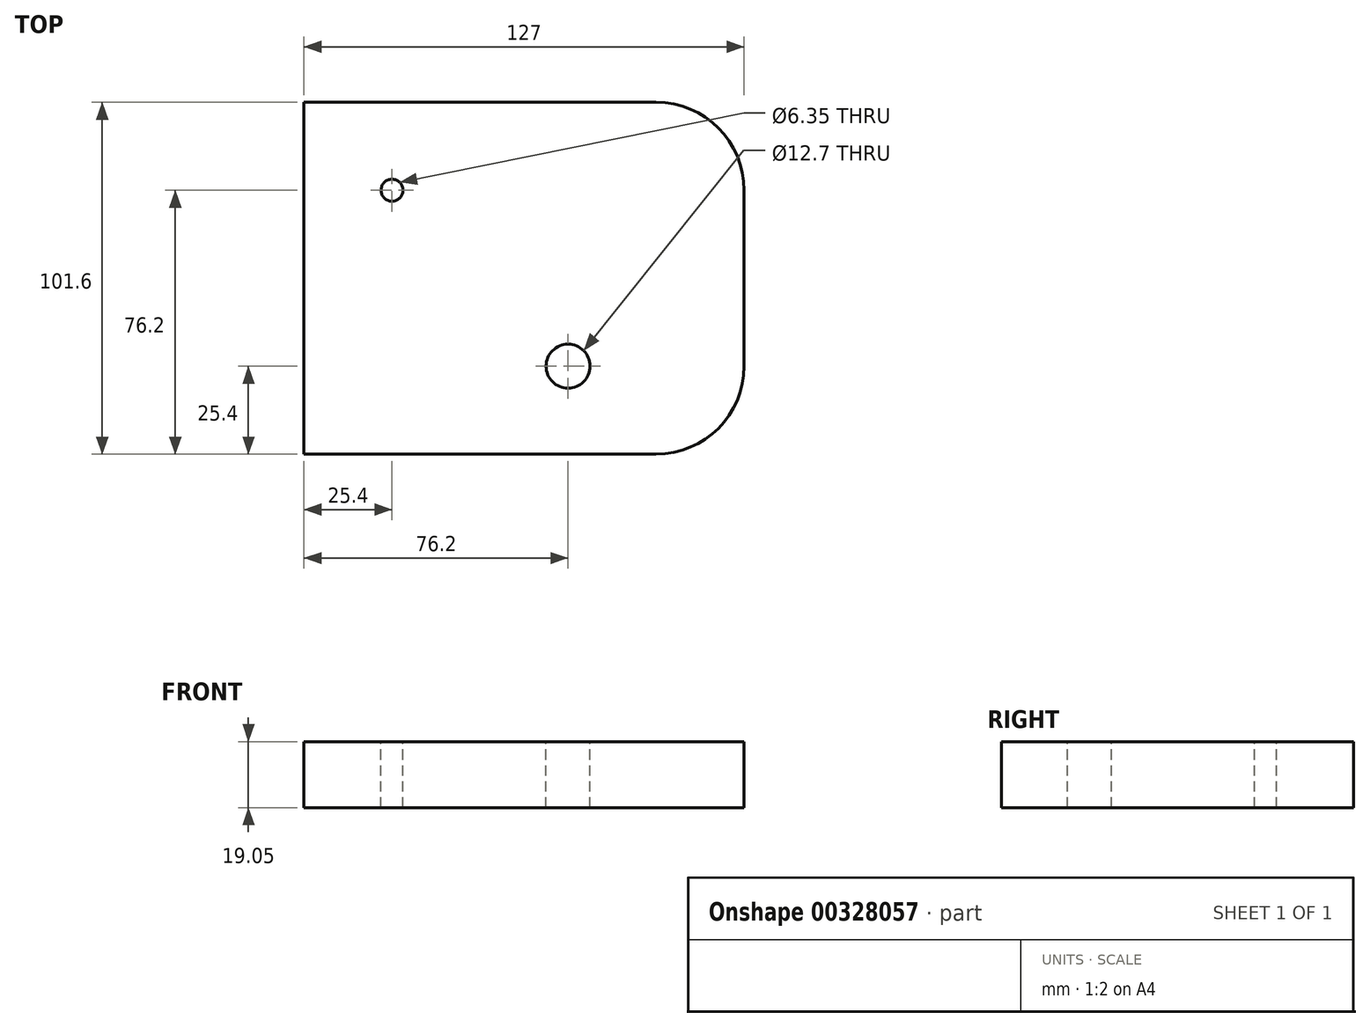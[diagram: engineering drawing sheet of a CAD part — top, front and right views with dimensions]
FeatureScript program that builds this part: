
annotation { "Feature Type Name" : "Feature", "Feature Type Description" : "" }
export const myFeature = defineFeature(function(context is Context, id is Id, definition is map)
    precondition{}
    {
        {
            var Q0;
            Q0=qCreatedBy(makeId("Top.planeOp"),FACE);
            var sketch = newSketch(context, id + "F0", { "sketchPlane" : qUnion([Q0])});
            skLineSegment(sketch, "E0.bottom", {"start": v(-63.5, 50.8) * mm, "end": v(63.5, 50.8) * mm});
            skLineSegment(sketch, "E0.top", {"start": v(-63.5, -50.8) * mm, "end": v(63.5, -50.8) * mm});
            skLineSegment(sketch, "E0.left", {"start": v(-63.5, 50.8) * mm, "end": v(-63.5, -50.8) * mm});
            skLineSegment(sketch, "E0.right", {"start": v(63.5, 50.8) * mm, "end": v(63.5, -50.8) * mm});
            skPoint(sketch, "E0.middle", {"position": v(0, 0) * mm});
            skSolve(sketch);
        }
        {
            var Q0;
            Q0=makeQuery(id+"F0.imprint","IMPRINT",FACE,{"disambiguationData":[TD([[makeQuery(id+"F0.imprint","IMPRINT",EDGE,{"derivedFrom":sQuery(id+"F0.wireOp",EDGE,"E0.bottom")}),-1.0]])]});
            extrude(context, id + "F1", {"entities" : qUnion([Q0]), "depth" : 19.05 * mm});
        }
        {
            var Q0;
            Q0=makeQuery(id+"F1.opExtrude","CAP_FACE",FACE,{"disambiguationData":[OSD([sQuery(id+"F0.wireOp",EDGE,"E0.bottom"),sQuery(id+"F0.wireOp",EDGE,"E0.top"),sQuery(id+"F0.wireOp",EDGE,"E0.left"),sQuery(id+"F0.wireOp",EDGE,"E0.right")])],"isStart":false});
            var sketch = newSketch(context, id + "F2", { "sketchPlane" : qUnion([Q0])});
            skCircle(sketch, "E1", {"center": v(-38.1, 25.4) * mm, "radius": 3.18 * mm});
            skSolve(sketch);
        }
        {
            var Q0;
            Q0=makeQuery(id+"F2.imprint","IMPRINT",FACE,{"disambiguationData":[TD([[makeQuery(id+"F2.imprint","IMPRINT",EDGE,{"derivedFrom":sQuery(id+"F2.wireOp",EDGE,"E1")}),1.0]])]});
            extrude(context, id + "F3", {"entities" : qUnion([Q0]), "operationType" : NewBodyOperationType.REMOVE, "oppositeDirection" : true, "depth" : 25.4 * mm});
        }
        {
            var Q0;
            Q0=makeQuery(id+"F1.opExtrude","CAP_FACE",FACE,{"disambiguationData":[OSD([sQuery(id+"F0.wireOp",EDGE,"E0.bottom"),sQuery(id+"F0.wireOp",EDGE,"E0.top"),sQuery(id+"F0.wireOp",EDGE,"E0.left"),sQuery(id+"F0.wireOp",EDGE,"E0.right")])],"isStart":false});
            var sketch = newSketch(context, id + "F4", { "sketchPlane" : qUnion([Q0])});
            skCircle(sketch, "E2", {"center": v(12.7, -25.4) * mm, "radius": 6.35 * mm});
            skSolve(sketch);
        }
        {
            var Q0;
            Q0=makeQuery(id+"F4.imprint","IMPRINT",FACE,{"disambiguationData":[TD([[makeQuery(id+"F4.imprint","IMPRINT",EDGE,{"derivedFrom":sQuery(id+"F4.wireOp",EDGE,"E2")}),1.0]])]});
            extrude(context, id + "F5", {"entities" : qUnion([Q0]), "operationType" : NewBodyOperationType.REMOVE, "oppositeDirection" : true, "depth" : 25.4 * mm});
        }
        {
            var Q0;
            Q0=makeQuery(id+"F1.opExtrude","SWEPT_EDGE",EDGE,{"disambiguationData":[OSD([sQuery(id+"F0.wireOp",EDGE,"E0.top"),sQuery(id+"F0.wireOp",EDGE,"E0.right")])]});
            var Q1;
            Q1=makeQuery(id+"F1.opExtrude","SWEPT_EDGE",EDGE,{"disambiguationData":[OSD([sQuery(id+"F0.wireOp",EDGE,"E0.bottom"),sQuery(id+"F0.wireOp",EDGE,"E0.right")])]});
            fillet(context, id + "F6", {"entities" : qUnion([Q0, Q1]), "radius" : 25.4 * mm, "tangentPropagation" : true, "allowEdgeOverflow" : false});
        }
    });
